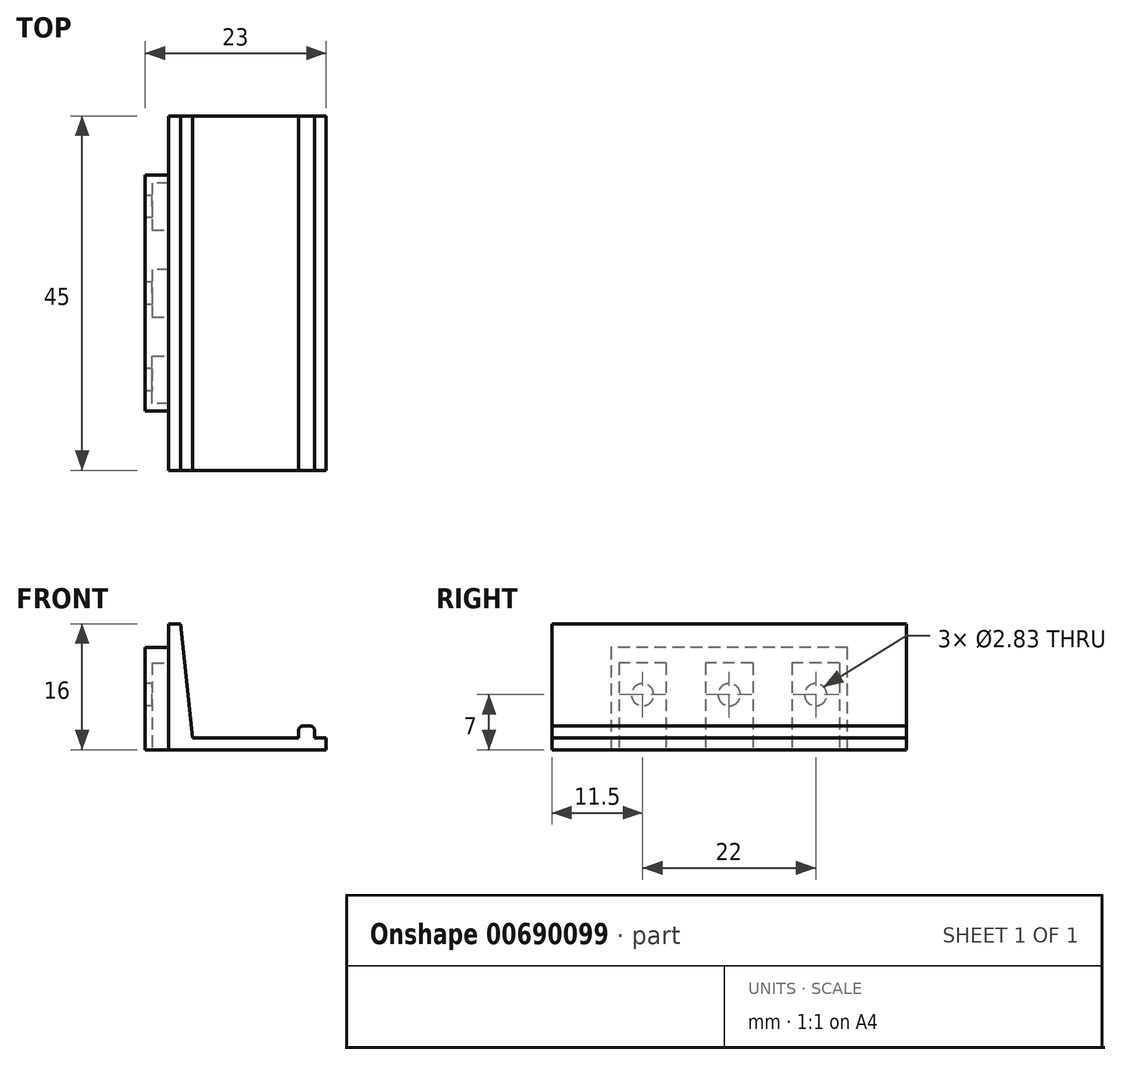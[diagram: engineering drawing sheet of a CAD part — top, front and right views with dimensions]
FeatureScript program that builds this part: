
annotation { "Feature Type Name" : "Feature", "Feature Type Description" : "" }
export const myFeature = defineFeature(function(context is Context, id is Id, definition is map)
    precondition{}
    {
        {
            var Q0;
            Q0=qCreatedBy(makeId("Front.planeOp"),FACE);
            var sketch = newSketch(context, id + "F0", { "sketchPlane" : qUnion([Q0])});
            skLineSegment(sketch, "E0", {"start": v(0, 0) * mm, "end": v(20, 0) * mm});
            skLineSegment(sketch, "E1", {"start": v(0, 0) * mm, "end": v(0, 16) * mm});
            skLineSegment(sketch, "E2", {"start": v(0, 16) * mm, "end": v(1.5, 16) * mm});
            skLineSegment(sketch, "E3", {"start": v(20, 0) * mm, "end": v(20, 1.5) * mm});
            skLineSegment(sketch, "E4", {"start": v(20, 1.5) * mm, "end": v(3, 1.5) * mm});
            skLineSegment(sketch, "E5", {"start": v(3, 1.5) * mm, "end": v(1.5, 16) * mm});
            skSolve(sketch);
        }
        {
            var Q0;
            Q0=makeQuery(id+"F0.imprint","IMPRINT",FACE,{"disambiguationData":[TD([[makeQuery(id+"F0.imprint","IMPRINT",EDGE,{"derivedFrom":sQuery(id+"F0.wireOp",EDGE,"E0")}),1.0]])]});
            extrude(context, id + "F1", {"entities" : qUnion([Q0]), "depth" : 45 * mm, "offsetDistance" : 25 * mm});
        }
        {
            var Q0;
            Q0=makeQuery(id+"F1.opExtrude","SWEPT_FACE",FACE,{"disambiguationData":[OSD([sQuery(id+"F0.wireOp",EDGE,"E1")])]});
            var sketch = newSketch(context, id + "F2", { "sketchPlane" : qUnion([Q0])});
            skLineSegment(sketch, "E6", {"start": v(0, 0) * mm, "end": v(7.5, 0) * mm});
            skLineSegment(sketch, "E7", {"start": v(7.5, 0) * mm, "end": v(7.5, 13) * mm});
            skLineSegment(sketch, "E8", {"start": v(7.5, 13) * mm, "end": v(37.5, 13) * mm});
            skLineSegment(sketch, "E9", {"start": v(37.5, 13) * mm, "end": v(37.5, 0) * mm});
            skSolve(sketch);
        }
        {
            var Q0;
            {var subQ0=sQuery(id+"F2.wireOp",EDGE,"E7");Q0=makeQuery(id+"F2.imprint","IMPRINT",FACE,{"disambiguationData":[TD([[makeQuery(id+"F2.imprint","IMPRINT",EDGE,{"derivedFrom":subQ0}),-1.0]])]});}
            extrude(context, id + "F3", {"entities" : qUnion([Q0]), "operationType" : NewBodyOperationType.ADD, "depth" : 3 * mm, "offsetDistance" : 25 * mm});
        }
        {
            var Q0;
            {var subQ0=sQuery(id+"F0.wireOp",EDGE,"E0");Q0=makeQuery(id+"F3.boolean.opBoolean","MERGE",FACE,{"derivedFrom":[makeQuery(id+"F1.opExtrude","SWEPT_FACE",FACE,{"disambiguationData":[OSD([subQ0])]}),makeQuery(id+"F3.opExtrude","SWEPT_FACE",FACE,{"disambiguationData":[OSD([subQ0,sQuery(id+"F0.wireOp",EDGE,"E1")])]})]});}
            var sketch = newSketch(context, id + "F4", { "sketchPlane" : qUnion([Q0])});
            skLineSegment(sketch, "E10", {"start": v(0, 37.5) * mm, "end": v(0, 36.5) * mm});
            skLineSegment(sketch, "E11", {"start": v(0, 36.5) * mm, "end": v(-2.1, 36.5) * mm});
            skLineSegment(sketch, "E12", {"start": v(-2.1, 36.5) * mm, "end": v(-2.1, 30.5) * mm});
            skLineSegment(sketch, "E13", {"start": v(-2.1, 30.5) * mm, "end": v(0, 30.5) * mm});
            skLineSegment(sketch, "E14", {"start": v(0, 30.5) * mm, "end": v(0, 36.5) * mm});
            skLineSegment(sketch, "E15", {"start": v(0, 30.5) * mm, "end": v(0, 28) * mm, "construction": true});
            skLineSegment(sketch, "E16", {"start": v(0, 28) * mm, "end": v(-3, 28) * mm, "construction": true});
            skLineSegment(sketch, "E17.MirrorCS", {"start": v(-2.1, 25.5) * mm, "end": v(0, 25.5) * mm});
            skLineSegment(sketch, "E18.MirrorCS", {"start": v(-2.1, 19.5) * mm, "end": v(-2.1, 25.5) * mm});
            skLineSegment(sketch, "E19.MirrorCS", {"start": v(0, 25.5) * mm, "end": v(0, 19.5) * mm});
            skLineSegment(sketch, "E20.MirrorCS", {"start": v(0, 19.5) * mm, "end": v(-2.1, 19.5) * mm});
            skLineSegment(sketch, "E21", {"start": v(-3, 37.5) * mm, "end": v(-3, 22.5) * mm, "construction": true});
            skLineSegment(sketch, "E22", {"start": v(-3, 22.5) * mm, "end": v(20, 22.5) * mm, "construction": true});
            skLineSegment(sketch, "E23.MirrorCS", {"start": v(-3, 7.5) * mm, "end": v(-3, 22.5) * mm, "construction": true});
            skLineSegment(sketch, "E24.MirrorCS", {"start": v(-2.1, 14.5) * mm, "end": v(0, 14.5) * mm});
            skLineSegment(sketch, "E25.MirrorCS", {"start": v(-2.1, 8.5) * mm, "end": v(-2.1, 14.5) * mm});
            skLineSegment(sketch, "E26.MirrorCS", {"start": v(0, 14.5) * mm, "end": v(0, 8.5) * mm});
            skLineSegment(sketch, "E27.MirrorCS", {"start": v(0, 8.5) * mm, "end": v(-2.1, 8.5) * mm});
            skSolve(sketch);
        }
        {
            var Q0;
            Q0 = qSketchRegion(id + "F4", true);
            extrude(context, id + "F5", {"entities" : qUnion([Q0]), "operationType" : NewBodyOperationType.REMOVE, "oppositeDirection" : true, "depth" : 11 * mm, "offsetDistance" : 25 * mm});
        }
        {
            var Q0;
            Q0=makeQuery(id+"F3.opExtrude","CAP_FACE",FACE,{"disambiguationData":[OSD([sQuery(id+"F0.wireOp",EDGE,"E0"),sQuery(id+"F0.wireOp",EDGE,"E1"),sQuery(id+"F2.wireOp",EDGE,"E7"),sQuery(id+"F2.wireOp",EDGE,"E8"),sQuery(id+"F2.wireOp",EDGE,"E9")])],"isStart":false});
            var sketch = newSketch(context, id + "F6", { "sketchPlane" : qUnion([Q0])});
            skLineSegment(sketch, "E28", {"start": v(37.5, 0) * mm, "end": v(37.5, 13) * mm});
            skLineSegment(sketch, "E29", {"start": v(37.5, 0) * mm, "end": v(37.5, 7) * mm, "construction": true});
            skLineSegment(sketch, "E30", {"start": v(37.5, 7) * mm, "end": v(36.5, 7) * mm, "construction": true});
            skLineSegment(sketch, "E31", {"start": v(36.5, 7) * mm, "end": v(33.5, 7) * mm, "construction": true});
            skPoint(sketch, "E32", {"position": v(33.5, 7) * mm});
            skLineSegment(sketch, "E33", {"start": v(37.5, 7) * mm, "end": v(22.5, 7) * mm, "construction": true});
            skLineSegment(sketch, "E34", {"start": v(22.5, 7) * mm, "end": v(22.5, 0) * mm, "construction": true});
            skPoint(sketch, "E35.MirrorP", {"position": v(11.5, 7) * mm});
            skPoint(sketch, "E36", {"position": v(22.5, 7) * mm});
            skSolve(sketch);
        }
        {
            var Q0;
            Q0=sQuery(id+"F6.wireOp",VERTEX,"E32");
            var Q1;
            Q1=sQuery(id+"F6.wireOp",VERTEX,"E36");
            var Q2;
            Q2=sQuery(id+"F6.wireOp",VERTEX,"E35.MirrorP");
            var Q3;
            Q3=makeQuery(id+"F1.opExtrude","SWEPT_BODY",BODY,{"disambiguationData":[OSD([sQuery(id+"F0.wireOp",EDGE,"E0"),sQuery(id+"F0.wireOp",EDGE,"EL2QgEpq-4ck6-Ab1S-ue7h-Xw9jDGvIvdB5"),sQuery(id+"F0.wireOp",EDGE,"iuUeco4B-E838-44TX-xQ0C-mgXBrXigQZKO"),sQuery(id+"F0.wireOp",EDGE,"E1"),sQuery(id+"F0.wireOp",EDGE,"E2"),sQuery(id+"F0.wireOp",EDGE,"j2UPf6uu-5WT3-3ISW-CCnG-hPzEJSS1Wr8w")])]});
            hole(context, id + "F7", {"style" : HoleStyle.SIMPLE, "endStyle" : HoleEndStyle.BLIND, "holeDiameter" : 2.83 * mm, "majorDiameter" : 5 * mm, "holeDepth" : 2 * mm, "isTappedThrough" : true, "tappedDepth" : 12 * mm, "tapClearance" : 3, "locations" : qUnion([Q0, Q1, Q2]), "scope" : qUnion([Q3])});
        }
        {
            var Q0;
            Q0=makeQuery(id+"F1.opExtrude","SWEPT_FACE",FACE,{"disambiguationData":[OSD([sQuery(id+"F0.wireOp",EDGE,"E4")])]});
            var sketch = newSketch(context, id + "F8", { "sketchPlane" : qUnion([Q0])});
            skLineSegment(sketch, "E37", {"start": v(20, 0) * mm, "end": v(18.5, 0) * mm, "construction": true});
            skLineSegment(sketch, "E38.bottom", {"start": v(18.5, 0) * mm, "end": v(16.5, 0) * mm});
            skLineSegment(sketch, "E38.top", {"start": v(18.5, -45) * mm, "end": v(16.5, -45) * mm});
            skLineSegment(sketch, "E38.left", {"start": v(18.5, 0) * mm, "end": v(18.5, -45) * mm});
            skLineSegment(sketch, "E38.right", {"start": v(16.5, 0) * mm, "end": v(16.5, -45) * mm});
            skSolve(sketch);
        }
        {
            var Q0;
            Q0=makeQuery(id+"F8.imprint","IMPRINT",FACE,{"disambiguationData":[TD([[makeQuery(id+"F8.imprint","IMPRINT",EDGE,{"derivedFrom":sQuery(id+"F8.wireOp",EDGE,"E38.bottom")}),1.0]])]});
            var Q1;
            Q1=sQuery(id+"F8.wireOp",EDGE,"E38.right");
            var Q2;
            Q2=sQuery(id+"F8.wireOp",EDGE,"E38.top");
            var Q3;
            Q3=sQuery(id+"F8.wireOp",EDGE,"E38.left");
            var Q4;
            Q4=sQuery(id+"F8.wireOp",EDGE,"E38.bottom");
            extrude(context, id + "F9", {"entities" : qUnion([Q0]), "operationType" : NewBodyOperationType.ADD, "surfaceEntities" : qUnion([Q1, Q2, Q3, Q4]), "depth" : 1.5 * mm, "offsetDistance" : 25 * mm});
        }
        {
            var Q0;
            Q0=makeQuery(id+"F9.opExtrude","CAP_EDGE",EDGE,{"disambiguationData":[OSD([sQuery(id+"F8.wireOp",EDGE,"E38.left")])],"isStart":false});
            var Q1;
            Q1=makeQuery(id+"F9.opExtrude","CAP_EDGE",EDGE,{"disambiguationData":[OSD([sQuery(id+"F8.wireOp",EDGE,"E38.right")])],"isStart":false});
            fillet(context, id + "F10", {"entities" : qUnion([Q0, Q1]), "radius" : 0.5 * mm, "tangentPropagation" : true, "allowEdgeOverflow" : false});
        }
    });
